# Revit family: Tub_Spout-American_Standard-Town_Square_S-8888111_Series
name_source: partatom
category: Plumbing Fixtures
units: mm (PartAtom-declared; Revit-internal decimal feet)

## family parameters
Cut with Voids When Loaded = No
Host = Face
OmniClass Number = 23.45.05.14.21
OmniClass Title = Bathtubs
Part Type = Normal
Room Calculation Point = No
Round Connector Dimension = Use Diameter
Shared = Yes

## types (4) — shared parameters
Assembly Code = D2020300
CW Connection = No
CWFU = 3
Default Elevation = 25"
Description = Non-Diverter 1/2" IPS Tub Spout
HW Connection = No
HWFU = 3
Height = 2 5/8"
Installation Type = Wall Mounted
Length = 7 5/16"
Manufacturer = American Standard
Price = Prices may vary. Please consult Manufacturer Representative for most up-to-date price list.
Product Documentation Link = https://www.americanstandard.ca
Product Page URL = https://www.americanstandard.ca
Revised Date = 11/18/2021
Tempered Water Connection = Yes
Tempered Water Connection Diameter = 1/2"
Tempered Water Connection Radius = 1/4"
Type Comments = Town Square S Slip-On Non-Diverter Tub Spout
URL = https://www.americanstandard.ca
Vent Connection = No
WFU = 4
Warranty Information = Limited Lifetime Function and Finish Warranty
Waste Connection = No
Width = 2 5/8"

## per-type parameters (varying)
| type | Finish | Material |
| 8888111.002 | Metal-American_Standard-002-Polished_Chrome | Metal-American Standard-002-Polished_Chrome |
| 8888111.295 | Metal-American_Standard-295-Brushed_Nickel(PVD) | Metal-American_Standard-295-Brushed_Nickel(PVD) |
| 8888111.013 | Metal-American_Standard-013-Polished Nickel | Metal-American_Standard-013-Polished Nickel |
| 8888111.278 | Metal-American_Standard-278-Legacy Bronze | Metal-American_Standard-278-Legacy Bronze |

note: column(s) folded — value = type name in every type: Model

## geometry (parser evidence)
native form markers: Sweep x3
no freeform markers — native parametric forms only
